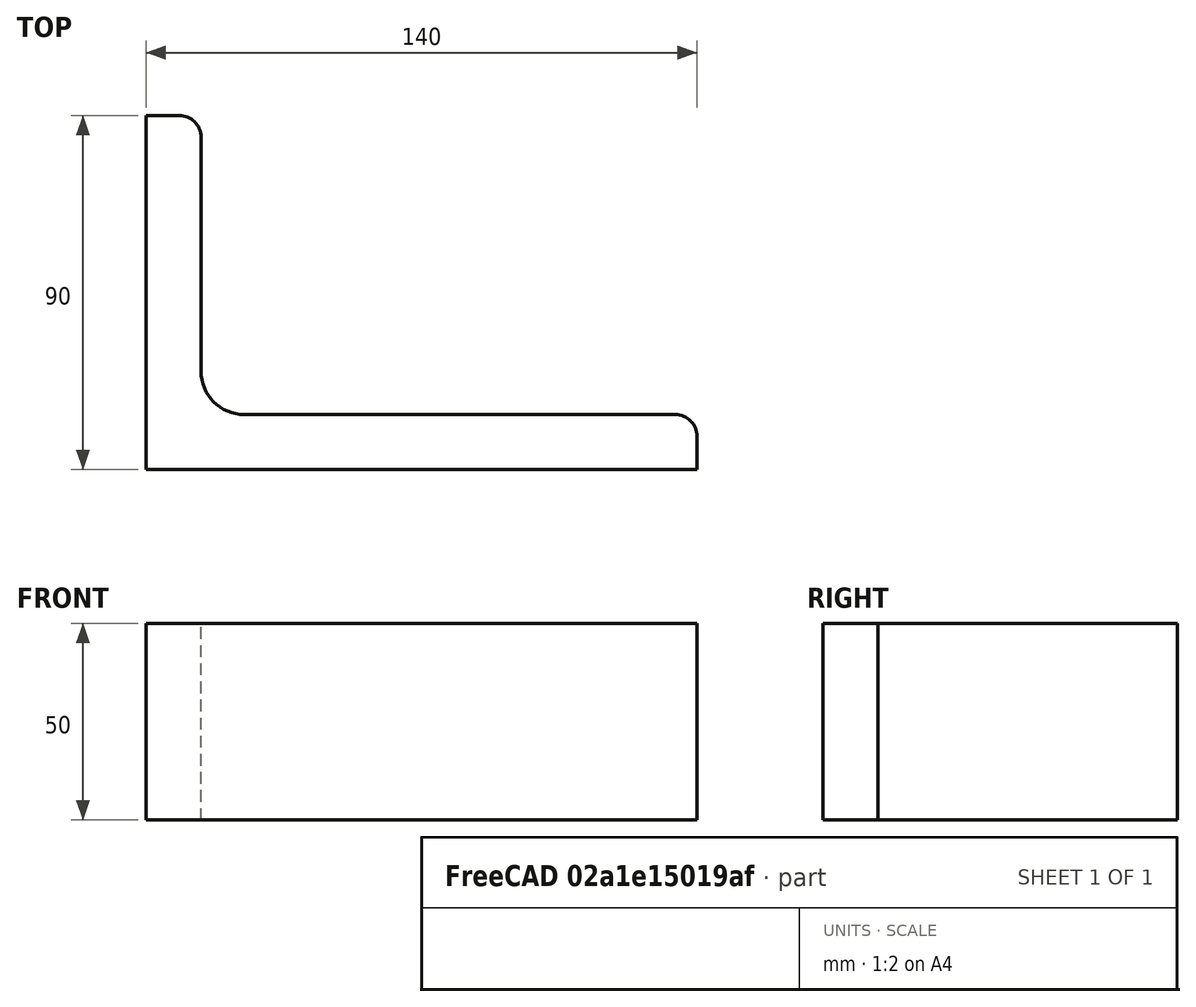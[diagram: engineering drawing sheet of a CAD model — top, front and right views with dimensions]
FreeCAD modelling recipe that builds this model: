
FCSTD DOCUMENT  (FreeCAD 0.15R4671 (Git))
Label: Angle Bar 140x90x14 EN10056 S235JR
License: All rights reserved
LicenseURL: http://en.wikipedia.org/wiki/All_rights_reserved
objects: Sketcher::SketchObject×1, Part::Extrusion×1
note: 2 computed .brp shape members not serialized (recipe doc carries the construction recipe); baked Part::Feature solids carry a one-line shape summary decoded from their .brp

FEATURE [Sketcher::SketchObject] Sketch
  sketch-geometry (9):
    g0: LineSegment StartX=0 StartY=0 StartZ=0 EndX=140 EndY=0 EndZ=0
    g1: LineSegment StartX=140 StartY=0 StartZ=0 EndX=140 EndY=8.5 EndZ=0
    g2: LineSegment StartX=134.5 StartY=14 StartZ=0 EndX=25 EndY=14 EndZ=0
    g3: LineSegment StartX=0 StartY=0 StartZ=0 EndX=0 EndY=90 EndZ=0
    g4: LineSegment StartX=0 StartY=90 StartZ=0 EndX=8.5 EndY=90 EndZ=0
    g5: LineSegment StartX=14 StartY=84.5 StartZ=0 EndX=14 EndY=25 EndZ=0
    g6: ArcOfCircle CenterX=25 CenterY=25 CenterZ=0 NormalX=0 NormalY=0 NormalZ=1 Radius=11 StartAngle=3.14159 EndAngle=4.71239
    g7: ArcOfCircle CenterX=8.5 CenterY=84.5 CenterZ=0 NormalX=0 NormalY=0 NormalZ=1 Radius=5.5 StartAngle=0 EndAngle=1.5708
    g8: ArcOfCircle CenterX=134.5 CenterY=8.5 CenterZ=0 NormalX=0 NormalY=0 NormalZ=1 Radius=5.5 StartAngle=0 EndAngle=1.5708
  constraints (23):
    c: Coincident(g0,g-1)
    c: Horizontal(g0)
    c: Coincident(g1,g0)
    c: Vertical(g1)
    c: Horizontal(g2)
    c: Coincident(g3,g-1)
    c: Vertical(g3)
    c: Coincident(g4,g3)
    c: Horizontal(g4)
    c: Vertical(g5)
    c: Tangent(g5,g6) = -1.5708
    c: Tangent(g2,g6) = 1.5708
    c: Tangent(g4,g7) = 1.5708
    c: Tangent(g5,g7) = 1.5708
    c: Tangent(g2,g8) = -1.5708
    c: Tangent(g1,g8) = -1.5708
    c: DistanceX(g0) = 140
    c: DistanceY(g3) = 90
    c: DistanceY(g0,g2) = 14
    c: DistanceX(g3,g5) = 14
    c: Radius(g6) = 11
    c: Radius(g8) = 5.5
    c: Radius(g7) = 5.5
FEATURE [Part::Extrusion] Extrude  label="Angle Bar 140x90x14 EN10056 S235JR"
  Base = -> Sketch
  Dir = (0,0,50)
  Solid = true
